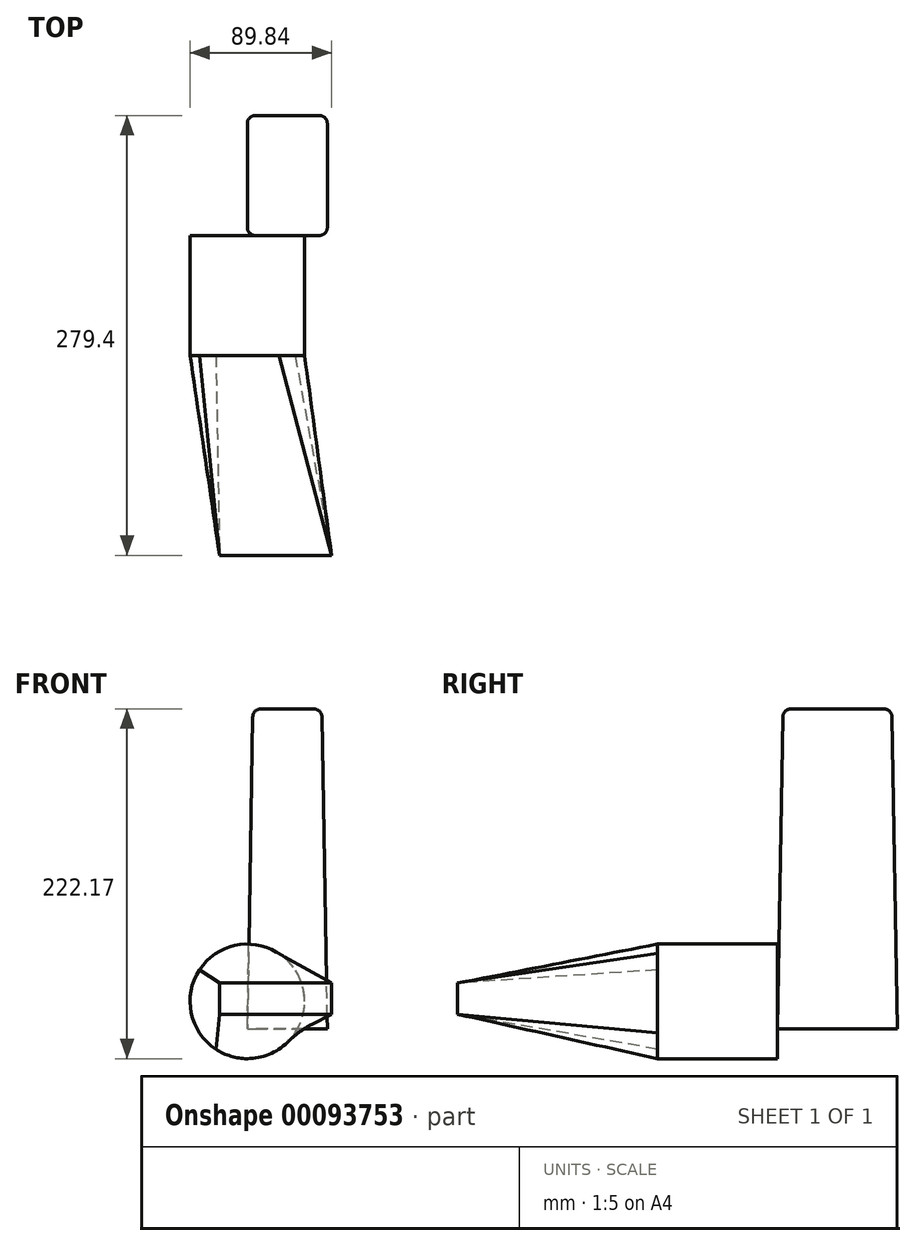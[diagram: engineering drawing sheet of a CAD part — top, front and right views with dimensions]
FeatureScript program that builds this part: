
annotation { "Feature Type Name" : "Feature", "Feature Type Description" : "" }
export const myFeature = defineFeature(function(context is Context, id is Id, definition is map)
    precondition{}
    {
        {
            var Q0;
            Q0=qCreatedBy(makeId("Top.planeOp"),FACE);
            var sketch = newSketch(context, id + "F0", { "sketchPlane" : qUnion([Q0])});
            skLineSegment(sketch, "E0.bottom", {"start": v(0, 0) * mm, "end": v(50.8, 0) * mm});
            skLineSegment(sketch, "E0.top", {"start": v(0, 76.2) * mm, "end": v(50.8, 76.2) * mm});
            skLineSegment(sketch, "E0.left", {"start": v(0, 0) * mm, "end": v(0, 76.2) * mm});
            skLineSegment(sketch, "E0.right", {"start": v(50.8, 0) * mm, "end": v(50.8, 76.2) * mm});
            skSolve(sketch);
        }
        {
            var Q0;
            Q0 = qSketchRegion(id + "F0", true);
            extrude(context, id + "F1", {"entities" : qUnion([Q0]), "depth" : 203.2 * mm, "hasDraft" : true, "draftAngle" : 1 * degree, "draftPullDirection" : true});
        }
        {
            var Q0;
            Q0=makeQuery(id+"F1.opExtrude","CAP_FACE",FACE,{"disambiguationData":[OSD([sQuery(id+"F0.wireOp",EDGE,"E0.bottom"),sQuery(id+"F0.wireOp",EDGE,"E0.top"),sQuery(id+"F0.wireOp",EDGE,"E0.left"),sQuery(id+"F0.wireOp",EDGE,"E0.right")])],"isStart":false});
            var Q1;
            Q1=makeQuery(id+"F1.opExtrude","SWEPT_EDGE",EDGE,{"disambiguationData":[OSD([sQuery(id+"F0.wireOp",EDGE,"E0.top"),sQuery(id+"F0.wireOp",EDGE,"E0.right")])]});
            var Q2;
            Q2=makeQuery(id+"F1.opExtrude","SWEPT_EDGE",EDGE,{"disambiguationData":[OSD([sQuery(id+"F0.wireOp",EDGE,"E0.top"),sQuery(id+"F0.wireOp",EDGE,"E0.left")])]});
            var Q3;
            Q3=makeQuery(id+"F1.opExtrude","SWEPT_EDGE",EDGE,{"disambiguationData":[OSD([sQuery(id+"F0.wireOp",EDGE,"E0.bottom"),sQuery(id+"F0.wireOp",EDGE,"E0.right")])]});
            var Q4;
            Q4=makeQuery(id+"F1.opExtrude","SWEPT_EDGE",EDGE,{"disambiguationData":[OSD([sQuery(id+"F0.wireOp",EDGE,"E0.bottom"),sQuery(id+"F0.wireOp",EDGE,"E0.left")])]});
            fillet(context, id + "F2", {"entities" : qUnion([Q0, Q1, Q2, Q3, Q4]), "radius" : 5.08 * mm, "tangentPropagation" : true, "allowEdgeOverflow" : false});
        }
        {
            var Q0;
            Q0=qCreatedBy(makeId("Front.planeOp"),FACE);
            cPlane(context, id + "F3", {"entities" : qUnion([Q0]), "cplaneType" : CPlaneType.OFFSET, "offset" : 76.2 * mm, "width" : 152.4 * mm, "height" : 152.4 * mm});
        }
        {
            var Q0;
            Q0=qCreatedBy(id+"F3.planeOp",FACE);
            cPlane(context, id + "F4", {"entities" : qUnion([Q0]), "cplaneType" : CPlaneType.OFFSET, "offset" : 127 * mm, "width" : 152.4 * mm, "height" : 152.4 * mm});
        }
        {
            var Q0;
            Q0=qCreatedBy(id+"F3.planeOp",FACE);
            var sketch = newSketch(context, id + "F5", { "sketchPlane" : qUnion([Q0])});
            skCircle(sketch, "E1", {"center": v(0, 17.4) * mm, "radius": 36.38 * mm});
            skSolve(sketch);
        }
        {
            var Q0;
            Q0=qCreatedBy(id+"F4.planeOp",FACE);
            var sketch = newSketch(context, id + "F6", { "sketchPlane" : qUnion([Q0])});
            skLineSegment(sketch, "E2.bottom", {"start": v(-17.62, 29.02) * mm, "end": v(53.46, 29.02) * mm});
            skLineSegment(sketch, "E2.top", {"start": v(-17.62, 9.28) * mm, "end": v(53.46, 9.28) * mm});
            skLineSegment(sketch, "E2.left", {"start": v(-17.62, 29.02) * mm, "end": v(-17.62, 9.28) * mm});
            skLineSegment(sketch, "E2.right", {"start": v(53.46, 29.02) * mm, "end": v(53.46, 9.28) * mm});
            skSolve(sketch);
        }
        {
            var Q0;
            Q0=makeQuery(id+"F5.imprint","IMPRINT",FACE,{"disambiguationData":[TD([[makeQuery(id+"F5.imprint","IMPRINT",EDGE,{"derivedFrom":sQuery(id+"F5.wireOp",EDGE,"E1")}),1.0]])]});
            var Q1;
            Q1=makeQuery(id+"F6.imprint","IMPRINT",FACE,{"disambiguationData":[TD([[makeQuery(id+"F6.imprint","IMPRINT",EDGE,{"derivedFrom":sQuery(id+"F6.wireOp",EDGE,"E2.bottom")}),-1.0]])]});
            loft(context, id + "F7", {"sheetProfilesArray" : [{ "sheetProfileEntities" : qUnion([Q0]) }, { "sheetProfileEntities" : qUnion([Q1]) }]});
        }
        {
            var Q0;
            Q0=qCreatedBy(makeId("Front.planeOp"),FACE);
            var sketch = newSketch(context, id + "F8", { "sketchPlane" : qUnion([Q0])});
            skCircle(sketch, "E3", {"center": v(0, 17.4) * mm, "radius": 36.38 * mm});
            skSolve(sketch);
        }
        {
            var Q0;
            Q0=makeQuery(id+"F8.imprint","IMPRINT",FACE,{"disambiguationData":[TD([[makeQuery(id+"F8.imprint","IMPRINT",EDGE,{"derivedFrom":sQuery(id+"F8.wireOp",EDGE,"E3")}),1.0]])]});
            var Q1;
            Q1 = qSketchRegion(id + "F5", true);
            loft(context, id + "F9", {"operationType" : NewBodyOperationType.ADD, "sheetProfilesArray" : [{ "sheetProfileEntities" : qUnion([Q0]) }, { "sheetProfileEntities" : qUnion([Q1]) }]});
        }
    });
